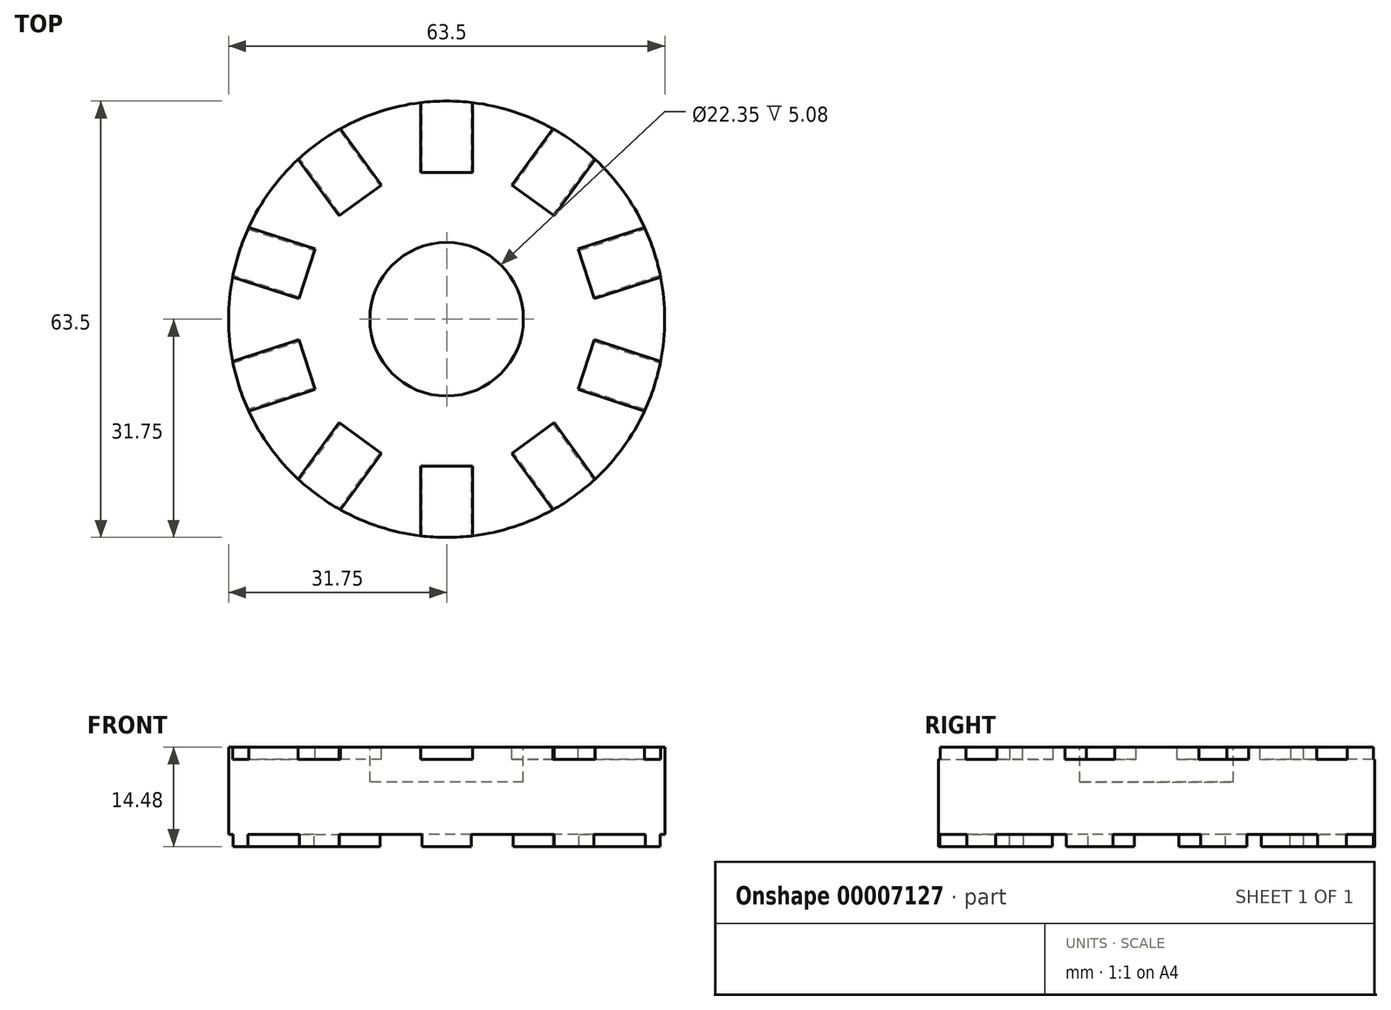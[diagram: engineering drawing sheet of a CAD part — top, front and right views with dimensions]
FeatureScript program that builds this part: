
annotation { "Feature Type Name" : "Feature", "Feature Type Description" : "" }
export const myFeature = defineFeature(function(context is Context, id is Id, definition is map)
    precondition{}
    {
        {
            var Q0;
            Q0=qCreatedBy(makeId("Top.planeOp"),FACE);
            var sketch = newSketch(context, id + "F0", { "sketchPlane" : qUnion([Q0])});
            skCircle(sketch, "E0", {"center": v(0, 0) * mm, "radius": 31.75 * mm});
            skSolve(sketch);
        }
        {
            var Q0;
            Q0=makeQuery(id+"F0.imprint","IMPRINT",FACE,{"disambiguationData":[TD([[makeQuery(id+"F0.imprint","IMPRINT",EDGE,{"derivedFrom":sQuery(id+"F0.wireOp",EDGE,"E0")}),1.0]])]});
            extrude(context, id + "F1", {"entities" : qUnion([Q0]), "depth" : 12.7 * mm});
        }
        {
            var Q0;
            Q0=makeQuery(id+"F1.opExtrude","CAP_FACE",FACE,{"disambiguationData":[OSD([sQuery(id+"F0.wireOp",EDGE,"E0")])],"isStart":false});
            var sketch = newSketch(context, id + "F2", { "sketchPlane" : qUnion([Q0])});
            skCircle(sketch, "E1", {"center": v(0, 0) * mm, "radius": 11.18 * mm});
            skSolve(sketch);
        }
        {
            var Q0;
            Q0=makeQuery(id+"F2.imprint","IMPRINT",FACE,{"disambiguationData":[TD([[makeQuery(id+"F2.imprint","IMPRINT",EDGE,{"derivedFrom":sQuery(id+"F2.wireOp",EDGE,"E1")}),1.0]])]});
            extrude(context, id + "F3", {"entities" : qUnion([Q0]), "operationType" : NewBodyOperationType.REMOVE, "oppositeDirection" : true, "depth" : 5.08 * mm});
        }
        {
            var Q0;
            Q0=makeQuery(id+"F1.opExtrude","CAP_FACE",FACE,{"disambiguationData":[OSD([sQuery(id+"F0.wireOp",EDGE,"E0")])],"isStart":false});
            var sketch = newSketch(context, id + "F4", { "sketchPlane" : qUnion([Q0])});
            skLineSegment(sketch, "E2", {"start": v(-3.81, -31.52) * mm, "end": v(-3.81, -21.36) * mm});
            skLineSegment(sketch, "E3", {"start": v(-3.81, -21.36) * mm, "end": v(3.81, -21.36) * mm});
            skLineSegment(sketch, "E4", {"start": v(3.81, -21.36) * mm, "end": v(3.81, -31.52) * mm});
            skPoint(sketch, "E5", {"position": v(0, -21.36) * mm});
            skSolve(sketch);
        }
        {
            var Q0;
            {var subQ2=sQuery(id+"F4.wireOp",EDGE,"E2");Q0=makeQuery(id+"F4.imprint","IMPRINT",FACE,{"disambiguationData":[TD([[makeQuery(id+"F4.imprint","IMPRINT",EDGE,{"derivedFrom":subQ2}),-1.0]])]});}
            extrude(context, id + "F5", {"entities" : qUnion([Q0]), "operationType" : NewBodyOperationType.REMOVE, "oppositeDirection" : true, "depth" : 1.78 * mm});
        }
        {
            var Q0;
            Q0=makeQuery(id+"F5.boolean.opBoolean","COPY",FACE,{"derivedFrom":makeQuery(id+"F5.opExtrude","CAP_FACE",FACE,{"disambiguationData":[OSD([sQuery(id+"F0.wireOp",EDGE,"E0"),sQuery(id+"F4.wireOp",EDGE,"E2"),sQuery(id+"F4.wireOp",EDGE,"E3"),sQuery(id+"F4.wireOp",EDGE,"E4")])],"isStart":false})});
            var Q1;
            Q1=makeQuery(id+"F5.boolean.opBoolean","COPY",FACE,{"derivedFrom":makeQuery(id+"F5.opExtrude","SWEPT_FACE",FACE,{"disambiguationData":[OSD([sQuery(id+"F4.wireOp",EDGE,"E4")])]})});
            var Q2;
            Q2=makeQuery(id+"F5.boolean.opBoolean","COPY",FACE,{"derivedFrom":makeQuery(id+"F5.opExtrude","SWEPT_FACE",FACE,{"disambiguationData":[OSD([sQuery(id+"F4.wireOp",EDGE,"E3")])]})});
            var Q3;
            Q3=makeQuery(id+"F5.boolean.opBoolean","COPY",FACE,{"derivedFrom":makeQuery(id+"F5.opExtrude","SWEPT_FACE",FACE,{"disambiguationData":[OSD([sQuery(id+"F4.wireOp",EDGE,"E2")])]})});
            var Q4;
            Q4=makeQuery(id+"F1.opExtrude","CAP_EDGE",EDGE,{"disambiguationData":[OSD([sQuery(id+"F0.wireOp",EDGE,"E0")])],"isStart":false});
            circularPattern(context, id + "F6", {"faces" : qUnion([Q0, Q1, Q2, Q3]), "axis" : qUnion([Q4]), "angle" : 36 * degree, "instanceCount" : 10, "patternType" : PatternType.FACE});
        }
        {
            var Q0;
            Q0=makeQuery(id+"F0.imprint","IMPRINT",FACE,{"disambiguationData":[TD([[makeQuery(id+"F0.imprint","IMPRINT",EDGE,{"derivedFrom":sQuery(id+"F0.wireOp",EDGE,"E0")}),1.0]])]});
            var sketch = newSketch(context, id + "F7", { "sketchPlane" : qUnion([Q0])});
            skLineSegment(sketch, "E6", {"start": v(-3.56, -31.55) * mm, "end": v(-3.56, -21.4) * mm});
            skLineSegment(sketch, "E7", {"start": v(-3.56, -21.4) * mm, "end": v(3.56, -21.4) * mm});
            skLineSegment(sketch, "E8", {"start": v(3.56, -21.4) * mm, "end": v(3.56, -31.55) * mm});
            skPoint(sketch, "E9", {"position": v(0, -21.4) * mm});
            skSolve(sketch);
        }
        {
            var Q0;
            {var subQ2=sQuery(id+"F7.wireOp",EDGE,"E6");Q0=makeQuery(id+"F7.imprint","IMPRINT",FACE,{"disambiguationData":[TD([[makeQuery(id+"F7.imprint","IMPRINT",EDGE,{"derivedFrom":subQ2}),-1.0]])]});}
            extrude(context, id + "F8", {"entities" : qUnion([Q0]), "operationType" : NewBodyOperationType.ADD, "oppositeDirection" : true, "depth" : 1.78 * mm});
        }
        {
            var Q0;
            Q0=makeQuery(id+"F8.opExtrude","CAP_FACE",FACE,{"disambiguationData":[OSD([sQuery(id+"F0.wireOp",EDGE,"E0"),sQuery(id+"F7.wireOp",EDGE,"E6"),sQuery(id+"F7.wireOp",EDGE,"E7"),sQuery(id+"F7.wireOp",EDGE,"E8")])],"isStart":false});
            var Q1;
            Q1=makeQuery(id+"F8.opExtrude","SWEPT_FACE",FACE,{"disambiguationData":[OSD([sQuery(id+"F7.wireOp",EDGE,"E8")])]});
            var Q2;
            Q2=makeQuery(id+"F8.opExtrude","SWEPT_FACE",FACE,{"disambiguationData":[OSD([sQuery(id+"F7.wireOp",EDGE,"E7")])]});
            var Q3;
            Q3=makeQuery(id+"F8.opExtrude","SWEPT_FACE",FACE,{"disambiguationData":[OSD([sQuery(id+"F7.wireOp",EDGE,"E6")])]});
            var Q4;
            Q4=sQuery(id+"F0.wireOp",EDGE,"E0");
            circularPattern(context, id + "F9", {"faces" : qUnion([Q0, Q1, Q2, Q3]), "axis" : qUnion([Q4]), "angle" : 36 * degree, "instanceCount" : 10, "patternType" : PatternType.FACE});
        }
    });
